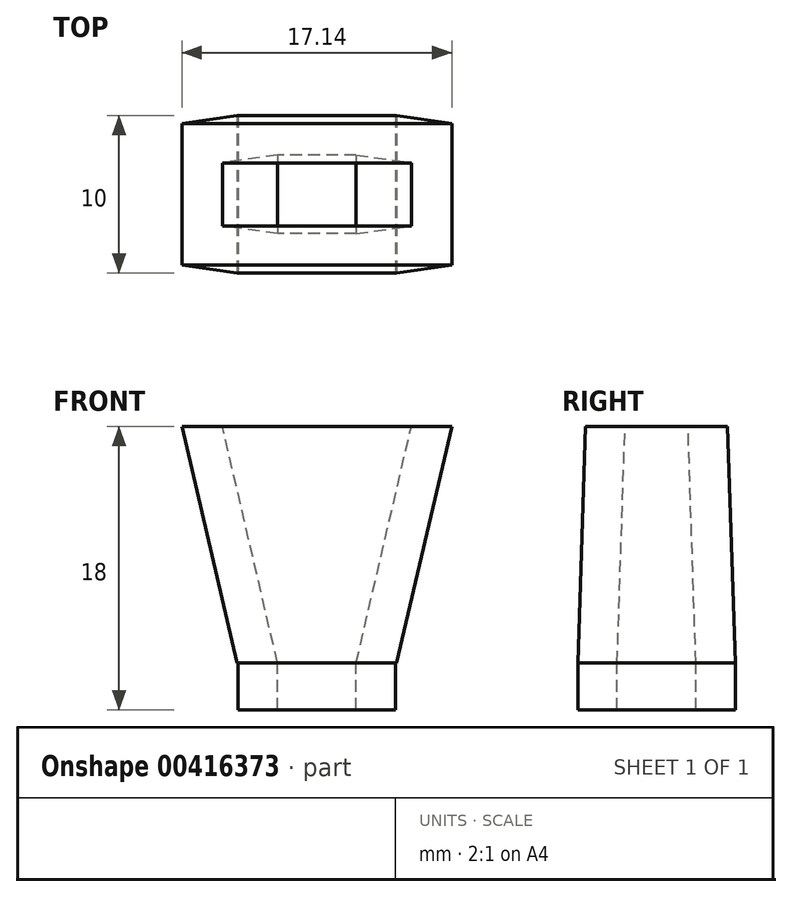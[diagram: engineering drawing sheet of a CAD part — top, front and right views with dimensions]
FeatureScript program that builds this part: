
annotation { "Feature Type Name" : "Feature", "Feature Type Description" : "" }
export const myFeature = defineFeature(function(context is Context, id is Id, definition is map)
    precondition{}
    {
        {
            var Q0;
            Q0=qCreatedBy(makeId("Top.planeOp"),FACE);
            var sketch = newSketch(context, id + "F0", { "sketchPlane" : qUnion([Q0])});
            skLineSegment(sketch, "E0.bottom", {"start": v(2.5, 2.5) * mm, "end": v(-2.5, 2.5) * mm});
            skLineSegment(sketch, "E0.top", {"start": v(2.5, -2.5) * mm, "end": v(-2.5, -2.5) * mm});
            skLineSegment(sketch, "E0.left", {"start": v(2.5, 2.5) * mm, "end": v(2.5, -2.5) * mm});
            skLineSegment(sketch, "E0.right", {"start": v(-2.5, 2.5) * mm, "end": v(-2.5, -2.5) * mm});
            skPoint(sketch, "E0.middle", {"position": v(0, 0) * mm});
            skCircle(sketch, "E1", {"center": v(0, 0) * mm, "radius": 10 * mm});
            skLineSegment(sketch, "E2.bottom", {"start": v(5, 5) * mm, "end": v(-5, 5) * mm});
            skLineSegment(sketch, "E2.top", {"start": v(5, -5) * mm, "end": v(-5, -5) * mm});
            skLineSegment(sketch, "E2.left", {"start": v(5, 5) * mm, "end": v(5, -5) * mm});
            skLineSegment(sketch, "E2.right", {"start": v(-5, 5) * mm, "end": v(-5, -5) * mm});
            skSolve(sketch);
        }
        {
            var Q0;
            Q0=qCreatedBy(makeId("Top.planeOp"),FACE);
            cPlane(context, id + "F1", {"entities" : qUnion([Q0]), "cplaneType" : CPlaneType.OFFSET, "offset" : 15 * mm, "width" : 150 * mm, "height" : 150 * mm});
        }
        {
            var Q0;
            Q0=qCreatedBy(id+"F1.planeOp",FACE);
            var sketch = newSketch(context, id + "F2", { "sketchPlane" : qUnion([Q0])});
            skLineSegment(sketch, "E3.bottom", {"start": v(6, -2) * mm, "end": v(-6, -2) * mm});
            skLineSegment(sketch, "E3.top", {"start": v(6, 2) * mm, "end": v(-6, 2) * mm});
            skLineSegment(sketch, "E3.left", {"start": v(6, -2) * mm, "end": v(6, 2) * mm});
            skLineSegment(sketch, "E3.right", {"start": v(-6, -2) * mm, "end": v(-6, 2) * mm});
            skPoint(sketch, "E3.middle", {"position": v(0, 0) * mm});
            skSolve(sketch);
        }
        {
            var Q0;
            Q0=makeQuery(id+"F0.imprint","IMPRINT",FACE,{"disambiguationData":[TD([[makeQuery(id+"F0.imprint","IMPRINT",EDGE,{"derivedFrom":sQuery(id+"F0.wireOp",EDGE,"E0.bottom")}),-1.0]])]});
            var Q1;
            Q1=makeQuery(id+"F0.imprint","IMPRINT",FACE,{"disambiguationData":[TD([[makeQuery(id+"F0.imprint","IMPRINT",EDGE,{"derivedFrom":sQuery(id+"F0.wireOp",EDGE,"E0.bottom")}),1.0]])]});
            var Q2;
            Q2=makeQuery(id+"F0.imprint","IMPRINT",FACE,{"disambiguationData":[TD([[makeQuery(id+"F0.imprint","IMPRINT",EDGE,{"derivedFrom":sQuery(id+"F0.wireOp",EDGE,"E1")}),1.0]])]});
            extrude(context, id + "F3", {"entities" : qUnion([Q0, Q1, Q2]), "depth" : 15 * mm});
        }
        {
            var Q1;
            Q1=makeQuery(id+"F0.imprint","IMPRINT",FACE,{"disambiguationData":[TD([[makeQuery(id+"F0.imprint","IMPRINT",EDGE,{"derivedFrom":sQuery(id+"F0.wireOp",EDGE,"E0.bottom")}),1.0]])]});
            var Q2;
            Q2=makeQuery(id+"F2.imprint","IMPRINT",FACE,{"disambiguationData":[TD([[makeQuery(id+"F2.imprint","IMPRINT",EDGE,{"derivedFrom":sQuery(id+"F2.wireOp",EDGE,"E3.bottom")}),-1.0]])]});
            loft(context, id + "F4", {"operationType" : NewBodyOperationType.REMOVE, "sheetProfilesArray" : [{ "sheetProfileEntities" : qUnion([Q1]) }, { "sheetProfileEntities" : qUnion([Q2]) }]});
        }
        {
            var Q0;
            Q0=makeQuery(id+"F3.opExtrude","SWEPT_FACE",FACE,{"disambiguationData":[OSD([sQuery(id+"F0.wireOp",EDGE,"E1")])]});
            var Q1;
            Q1=makeQuery(id+"F3.opExtrude","CAP_FACE",FACE,{"disambiguationData":[OSD([sQuery(id+"F0.wireOp",EDGE,"E1")])],"isStart":true});
            var Q2;
            Q2=makeQuery(id+"F3.opExtrude","CAP_FACE",FACE,{"disambiguationData":[OSD([sQuery(id+"F0.wireOp",EDGE,"E1")])],"isStart":false});
            shell(context, id + "F5", {"entities" : qUnion([Q0, Q1, Q2]), "thickness" : 2.5 * mm});
        }
        {
            var Q0;
            Q0=makeQuery(id+"F0.imprint","IMPRINT",FACE,{"disambiguationData":[TD([[makeQuery(id+"F0.imprint","IMPRINT",EDGE,{"derivedFrom":sQuery(id+"F0.wireOp",EDGE,"E0.bottom")}),-1.0]])]});
            extrude(context, id + "F6", {"entities" : qUnion([Q0]), "operationType" : NewBodyOperationType.ADD, "oppositeDirection" : true, "depth" : 3 * mm});
        }
    });
